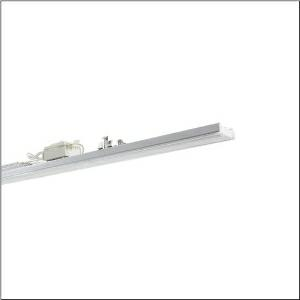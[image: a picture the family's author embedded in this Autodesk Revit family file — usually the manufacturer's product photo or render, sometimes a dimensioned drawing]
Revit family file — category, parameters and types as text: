
# Revit family: licross_r__21_recessed_mo_52te10dv4e5g_8208
name_source: partatom
category: Lighting Fixtures
units: mm (PartAtom-declared; Revit-internal decimal feet)

## family parameters
Cut with Voids When Loaded = No
Host = Face
Light Source = No
Part Type = Normal
Room Calculation Point = No
Round Connector Dimension = Use Diameter
Shared = No

## types (1)
- --- (1 x LED, 14990 lm, 85.3 W, 4000K)
    Apparent Load = 85 VA
    CIE Flux Codes = 50 81 96 100 100
    Color Rendering = 80
    Color Temperature = 4000K
    Default Elevation = 1800 mm
    Description = Licross® 21 Recessed MO, luminaire insert, of sheet steel, galvanised, coil coated, white, length: 2.250mm, width: 66mm, height: 67mm, LED rated luminous flux: 14.990lm, light colour: 840, control gear: DALI 2, with plug, 5-pole, with phase selection, mains connection: 220..240V, AC, 50/60Hz, rated input power: 85W, internal wiring halogen-free, primary optical cover: cover, of PMMA, light emission: direct distribution, primary light characteristic: symmetric, protection rating (complete): IP54, insulation class (complete): insulation class I (protective earthing), certification: CE, ENEC, VDE, UKCA, protection symbol: D if used in an environment with non-conductive dust loads with corresponding accessories, impact resistance: IK06, permissible ambient temperature for indoor applications: -25..+35°C, corresponds to IFS (International Featured Standards) requirements for safety and quality in the food industry, reducing of maximum allowable ambient temperature of 5°C with ceiling mounting, LABS conformity tested according to VDMA 24364:2018-05, packaging unit: 1 piece
    Height = 58 mm
    Lamp = 1 x LED
    Lamp Light Flux = 14990 lm
    Lamp Power = 85.3 W
    Lamp count = 1
    Length = 2250 mm
    Luminous efficacy = 176 lm/W
    Manufacturer = Siteco
    ModVariant = No
    Model = 52TE10DV4E5G
    Mounting Place = Ceiling
    Mounting Type = Pendant
    Number of Poles = 1
    OnlyDefault = Yes
    Power Factor = 1
    Product Name = Licross® 21 Recessed MO
    Product group = luminaire insert | ceiling pendant
    ProductGroupID = 902
    Protection Class = Protection class I
    Protection Degree = IP 54
    RLX_Detail_Level = 1
    RLX_Emergency_Light_Flux = 0 lm
    RLX_Emergency_Type = 0
    RLX_Emergency_Type_DB = No
    RlxData = <blob elided: 29625 chars, md5=7c4fc6a9>
    Socket = socket
    Standby Power = 0 W
    System Light Flux = 14990 lm
    System Power = 85 W
    Type Comments = factory setting: luminous flux: 100 % | dim-lin: 254 | 390 mA
    Type Image = l_1296930.jpg
    URL = http://relux.com
    VarID = @adj_149113
    Voltage = 0 V
    Weight = 0.00 kg
    Width = 66 mm

## geometry (parser evidence)
native form markers: Blend x4, Sweep x9
no freeform markers — native parametric forms only
